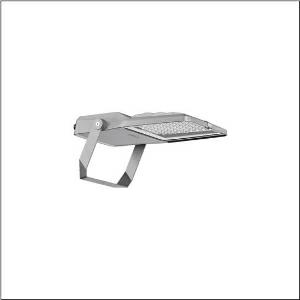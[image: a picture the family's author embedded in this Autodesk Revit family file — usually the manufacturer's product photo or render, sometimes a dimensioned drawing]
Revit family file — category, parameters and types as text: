
# Revit family: floodlight_fl_21_mini___pl52_5xa7776c2d1a_43f3
name_source: partatom
category: Lighting Fixtures
units: mm (PartAtom-declared; Revit-internal decimal feet)

## family parameters
Cut with Voids When Loaded = No
Host = Face
Light Source = No
Part Type = Normal
Room Calculation Point = No
Round Connector Dimension = Use Diameter
Shared = No

## types (1)
- --- (1 x LED, 12190 lm, 89 W, 3000K)
    Apparent Load = 89 VA
    CIE Flux Codes = 26 60 98 100 100
    Color Rendering = 70
    Color Temperature = 3000K
    Default Elevation = 1800 mm
    Description = Floodlight FL 21 mini, floodlight, primary light control with lens, of PMMA, primary optical cover: protective disc, of toughened safety glass, transparent, light distribution: PL52, light emission: direct distribution, installation type: surface-mounted, LED, High Power LED, rated luminous flux: 12.190lm, luminous efficacy: 137lm/W, light colour: 730, colour temperature: 3000K, control gear: Smart Interface (Zhaga), control: flexible luminous flux parameterisation, time-dependent luminous flux control, constant luminous flux control, overheat protection, pre-setting: logarithmic dimming characteristic, with terminal, 6-pole, mains connection: 220..240V, AC, 50/60Hz, start of lifetime: 89W, end of service life: 94W, reduction: 43W, luminaire housing, of diecast aluminium, powder-coated, Siteco® metallic grey (DB 702S), corrosivity category C5 mid according to DIN EN ISO 12944, suitable for swimming pools, chlorine-resistant, sealing non-destructively replaceable, mounting bracket, of steel, galvanised, powder-coated, Siteco® metallic grey (DB 702S), Smart Interface below and above, protection rating (complete): IP66, insulation class (complete): insulation class II (safety insulation), certification: CE, ENEC, VDE, protection symbol: D, impact resistance: IK08, permissible operating ambient temperature: -40..+40°C, permissible operating ambient temperature for outdoor applications: -40..+50°C, standard: DIN EN 12944, LABS conformity tested according to VDMA 24364:2018-05, packaging unit: 1 piece

Light Distribution: PL52
    Height = 70 mm
    Lamp = 1 x LED
    Lamp Light Flux = 12190 lm
    Lamp Power = 89 W
    Lamp count = 1
    Length = 485 mm
    Luminous efficacy = 137 lm/W
    Manufacturer = Siteco
    ModVariant = No
    Model = 5XA7776C2D1A
    Number of Poles = 1
    OnlyDefault = Yes
    Power Factor = 1
    Product Name = Floodlight FL 21 mini | PL52
    Product group = floodlight | pylon annexe
    ProductGroupID = 6201
    Protection Class = Protection class II
    Protection Degree = IP 66
    RLX_Detail_Level = 1
    RLX_Emergency_Light_Flux = 0 lm
    RLX_Emergency_Type = 0
    RLX_Emergency_Type_DB = No
    RlxData = <blob elided: 96145 chars, md5=b6192c16>
    Socket = socket
    Standby Power = 0 W
    System Light Flux = 12190 lm
    System Power = 89 W
    Type Comments = factory setting: luminous flux: 100 % | dim-lin: 254 | 456 mA
    Type Image = l_1006845.jpg
    URL = http://relux.com
    VarID = @adj_184741
    Voltage = 0 V
    Weight = 0.00 kg
    Width = 337 mm

## geometry (parser evidence)
native form markers: Blend x4, Sweep x12
no freeform markers — native parametric forms only
